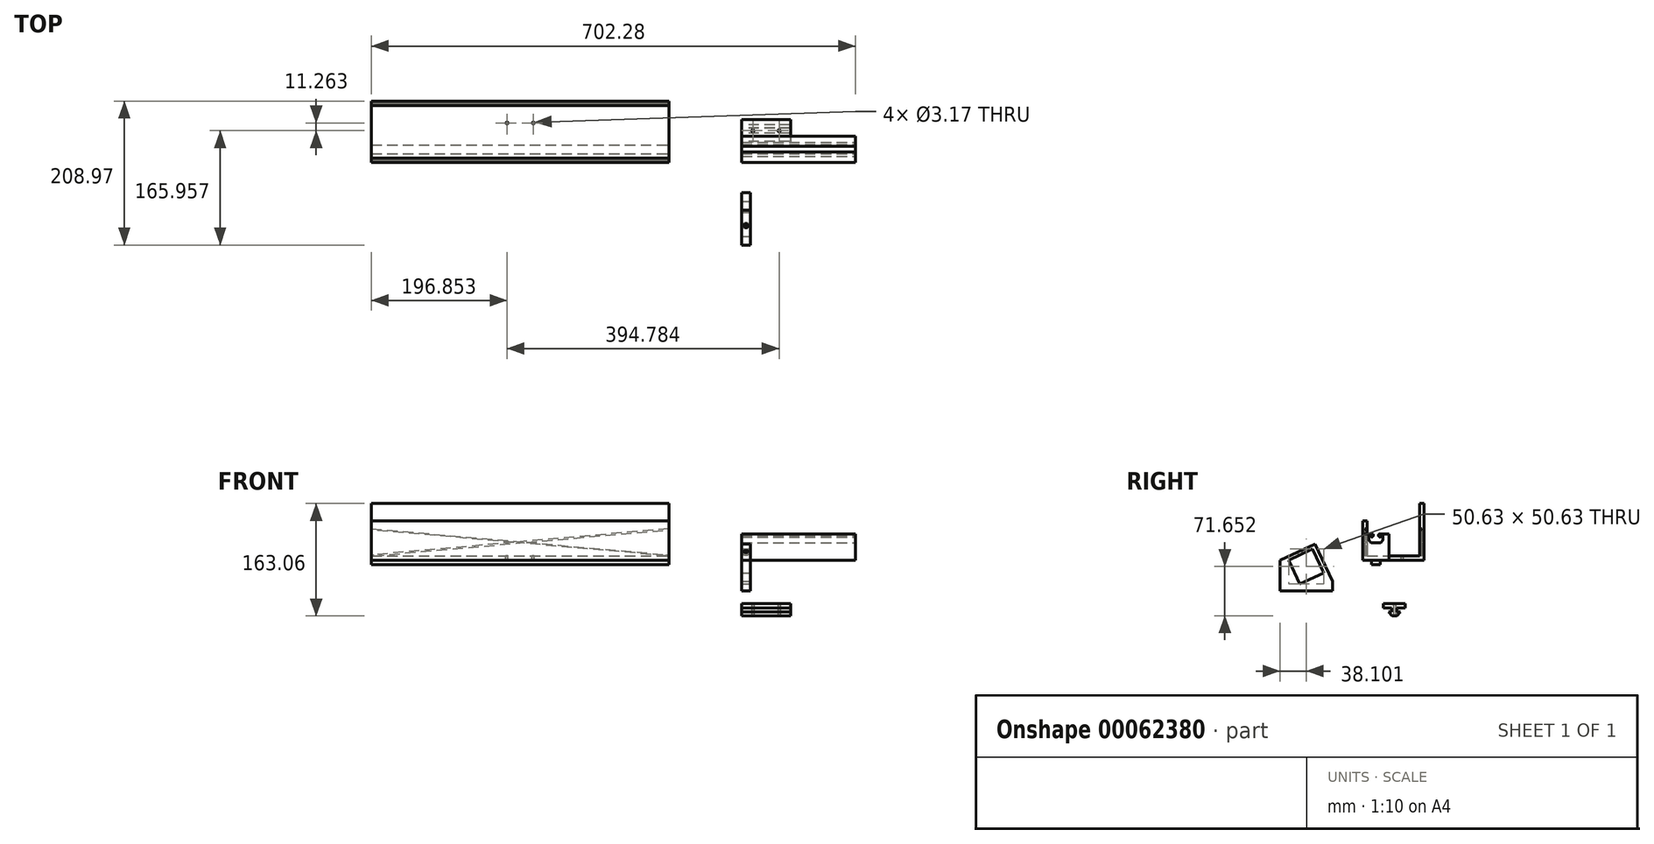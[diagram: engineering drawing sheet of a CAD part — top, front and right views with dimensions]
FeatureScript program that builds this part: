
annotation { "Feature Type Name" : "Feature", "Feature Type Description" : "" }
export const myFeature = defineFeature(function(context is Context, id is Id, definition is map)
    precondition{}
    {
        {
            var Q0;
            Q0=qCreatedBy(makeId("Right.planeOp"),FACE);
            var sketch = newSketch(context, id + "F0", { "sketchPlane" : qUnion([Q0])});
            skLineSegment(sketch, "E0.bottom", {"start": v(0, 0) * mm, "end": v(38.1, 0) * mm});
            skLineSegment(sketch, "E0.top", {"start": v(0, 38.1) * mm, "end": v(38.1, 38.1) * mm});
            skLineSegment(sketch, "E0.left", {"start": v(0, 0) * mm, "end": v(0, 38.1) * mm});
            skLineSegment(sketch, "E0.right", {"start": v(38.1, 0) * mm, "end": v(38.1, 38.1) * mm});
            skSolve(sketch);
        }
        {
            var Q0;
            Q0=makeQuery(id+"F0.imprint","IMPRINT",FACE,{"disambiguationData":[TD([[makeQuery(id+"F0.imprint","IMPRINT",EDGE,{"derivedFrom":sQuery(id+"F0.wireOp",EDGE,"E0.bottom")}),1.0]])]});
            extrude(context, id + "F1", {"entities" : qUnion([Q0]), "depth" : 165.1 * mm});
        }
        {
            var Q0;
            Q0=qCreatedBy(makeId("Top.planeOp"),FACE);
            var sketch = newSketch(context, id + "F2", { "sketchPlane" : qUnion([Q0])});
            skLineSegment(sketch, "E1.bottom", {"start": v(-105.38, 0) * mm, "end": v(-537.18, 0) * mm});
            skLineSegment(sketch, "E1.top", {"start": v(-105.38, 88.9) * mm, "end": v(-537.18, 88.9) * mm});
            skLineSegment(sketch, "E1.left", {"start": v(-105.38, 0) * mm, "end": v(-105.38, 88.9) * mm});
            skLineSegment(sketch, "E1.right", {"start": v(-537.18, 0) * mm, "end": v(-537.18, 88.9) * mm});
            skLineSegment(sketch, "E2", {"start": v(-537.18, 82.55) * mm, "end": v(-105.38, 82.55) * mm});
            skLineSegment(sketch, "E3", {"start": v(-537.18, 6.35) * mm, "end": v(-105.38, 6.35) * mm});
            skSolve(sketch);
        }
        {
            var Q0;
            Q0=qSketchRegion(id+"F2",true);
            extrude(context, id + "F3", {"entities" : qUnion([Q0]), "depth" : 6.35 * mm});
        }
        {
            var Q0;
            Q0=makeQuery(id+"F3.opExtrude","CAP_FACE",FACE,{"disambiguationData":[OSD([sQuery(id+"F2.wireOp",EDGE,"E1.bottom"),sQuery(id+"F2.wireOp",EDGE,"E1.top"),sQuery(id+"F2.wireOp",EDGE,"E1.left"),sQuery(id+"F2.wireOp",EDGE,"E1.right")])],"isStart":false});
            var sketch = newSketch(context, id + "F4", { "sketchPlane" : qUnion([Q0])});
            skLineSegment(sketch, "E4.bottom", {"start": v(-537.18, 88.9) * mm, "end": v(-105.38, 88.9) * mm});
            skLineSegment(sketch, "E4.top", {"start": v(-537.18, 82.55) * mm, "end": v(-105.38, 82.55) * mm});
            skLineSegment(sketch, "E4.left", {"start": v(-537.18, 88.9) * mm, "end": v(-537.18, 82.55) * mm});
            skLineSegment(sketch, "E4.right", {"start": v(-105.38, 88.9) * mm, "end": v(-105.38, 82.55) * mm});
            skSolve(sketch);
        }
        {
            var Q0;
            Q0=makeQuery(id+"F4.imprint","IMPRINT",FACE,{"disambiguationData":[TD([[makeQuery(id+"F4.imprint","IMPRINT",EDGE,{"derivedFrom":sQuery(id+"F4.wireOp",EDGE,"E4.bottom")}),1.0]])]});
            extrude(context, id + "F5", {"entities" : qUnion([Q0]), "operationType" : NewBodyOperationType.ADD, "depth" : 76.2 * mm});
        }
        {
            var Q0;
            Q0=makeQuery(id+"F3.opExtrude","CAP_FACE",FACE,{"disambiguationData":[OSD([sQuery(id+"F2.wireOp",EDGE,"E1.bottom"),sQuery(id+"F2.wireOp",EDGE,"E1.top"),sQuery(id+"F2.wireOp",EDGE,"E1.left"),sQuery(id+"F2.wireOp",EDGE,"E1.right")])],"isStart":false});
            var sketch = newSketch(context, id + "F6", { "sketchPlane" : qUnion([Q0])});
            skLineSegment(sketch, "E5.bottom", {"start": v(-537.18, 0) * mm, "end": v(-105.38, 0) * mm});
            skLineSegment(sketch, "E5.top", {"start": v(-537.18, 6.35) * mm, "end": v(-105.38, 6.35) * mm});
            skLineSegment(sketch, "E5.left", {"start": v(-537.18, 0) * mm, "end": v(-537.18, 6.35) * mm});
            skLineSegment(sketch, "E5.right", {"start": v(-105.38, 0) * mm, "end": v(-105.38, 6.35) * mm});
            skSolve(sketch);
        }
        {
            var Q0;
            Q0=makeQuery(id+"F6.imprint","IMPRINT",FACE,{"disambiguationData":[TD([[makeQuery(id+"F6.imprint","IMPRINT",EDGE,{"derivedFrom":sQuery(id+"F6.wireOp",EDGE,"E5.bottom")}),-1.0]])]});
            extrude(context, id + "F7", {"entities" : qUnion([Q0]), "operationType" : NewBodyOperationType.ADD, "depth" : 50.8 * mm});
        }
        {
            var Q0;
            Q0=makeQuery(id+"F5.opExtrude","SWEPT_FACE",FACE,{"disambiguationData":[OSD([sQuery(id+"F4.wireOp",EDGE,"E4.top")])]});
            var sketch = newSketch(context, id + "F8", { "sketchPlane" : qUnion([Q0])});
            skLineSegment(sketch, "E6", {"start": v(-537.18, 44.45) * mm, "end": v(-105.38, 6.35) * mm});
            skLineSegment(sketch, "E7", {"start": v(-105.38, 6.35) * mm, "end": v(-105.38, 7.94) * mm});
            skLineSegment(sketch, "E8", {"start": v(-105.38, 7.94) * mm, "end": v(-537.18, 46.04) * mm});
            skLineSegment(sketch, "E9", {"start": v(-537.18, 46.04) * mm, "end": v(-537.18, 44.45) * mm});
            skLineSegment(sketch, "E10", {"start": v(-108.54, 8.22) * mm, "end": v(-108.68, 6.64) * mm});
            skLineSegment(sketch, "E11", {"start": v(-321.28, 82.55) * mm, "end": v(-321.28, 6.35) * mm, "construction": true});
            skLineSegment(sketch, "E12.MirrorCS", {"start": v(-537.18, 7.94) * mm, "end": v(-105.38, 46.04) * mm});
            skLineSegment(sketch, "E13.MirrorCS", {"start": v(-105.38, 44.45) * mm, "end": v(-537.18, 6.35) * mm});
            skLineSegment(sketch, "E14.MirrorCS", {"start": v(-534.01, 8.22) * mm, "end": v(-533.87, 6.64) * mm});
            skSolve(sketch);
        }
        {
            var Q0;
            {var subQ0=sQuery(id+"F8.wireOp",EDGE,"E9");Q0=makeQuery(id+"F8.imprint","IMPRINT",FACE,{"disambiguationData":[TD([[makeQuery(id+"F8.imprint","IMPRINT",EDGE,{"derivedFrom":subQ0}),1.0]])]});}
            var Q1;
            {var subQ0=sQuery(id+"F8.wireOp",EDGE,"E13.MirrorCS");var subQ1=sQuery(id+"F8.wireOp",EDGE,"E8");var subQ2=makeQuery(id+"F8.imprint","INTERSECT",VERTEX,{"derivedFrom":[subQ1,subQ0]});Q1=makeQuery(id+"F8.imprint","IMPRINT",FACE,{"disambiguationData":[TD([[makeQuery(id+"F8.imprint","IMPRINT",EDGE,{"disambiguationData":[TD([[subQ2,-1.0]])],"derivedFrom":subQ1}),-1.0]])]});}
            var Q2;
            {var subQ0=sQuery(id+"F8.wireOp",EDGE,"E10");Q2=makeQuery(id+"F8.imprint","IMPRINT",FACE,{"disambiguationData":[TD([[makeQuery(id+"F8.imprint","IMPRINT",EDGE,{"derivedFrom":subQ0}),-1.0]])]});}
            var Q3;
            {var subQ0=sQuery(id+"F8.wireOp",EDGE,"E12.MirrorCS");var subQ1=sQuery(id+"F8.wireOp",EDGE,"E6");var subQ2=makeQuery(id+"F8.imprint","INTERSECT",VERTEX,{"derivedFrom":[subQ1,subQ0]});Q3=makeQuery(id+"F8.imprint","IMPRINT",FACE,{"disambiguationData":[TD([[makeQuery(id+"F8.imprint","IMPRINT",EDGE,{"disambiguationData":[TD([[subQ2,-1.0]])],"derivedFrom":subQ1}),1.0]])]});}
            var Q4;
            {var subQ5=sQuery(id+"F8.wireOp",EDGE,"E14.MirrorCS");Q4=makeQuery(id+"F8.imprint","IMPRINT",FACE,{"disambiguationData":[TD([[makeQuery(id+"F8.imprint","IMPRINT",EDGE,{"derivedFrom":subQ5}),1.0]])]});}
            extrude(context, id + "F9", {"entities" : qUnion([Q0, Q1, Q2, Q3, Q4]), "operationType" : NewBodyOperationType.REMOVE, "oppositeDirection" : true, "depth" : 3.17 * mm, "hasSecondDirection" : true, "secondDirectionOppositeDirection" : false, "secondDirectionDepth" : 79.38 * mm});
        }
        {
            var Q0;
            Q0=makeQuery(id+"F3.opExtrude","CAP_FACE",FACE,{"disambiguationData":[OSD([sQuery(id+"F2.wireOp",EDGE,"E1.bottom"),sQuery(id+"F2.wireOp",EDGE,"E1.top"),sQuery(id+"F2.wireOp",EDGE,"E1.left"),sQuery(id+"F2.wireOp",EDGE,"E1.right")])],"isStart":true});
            var sketch = newSketch(context, id + "F10", { "sketchPlane" : qUnion([Q0])});
            skLineSegment(sketch, "E15.bottom", {"start": v(-537.18, -25.4) * mm, "end": v(-105.38, -25.4) * mm});
            skLineSegment(sketch, "E15.top", {"start": v(-537.18, -12.7) * mm, "end": v(-105.38, -12.7) * mm});
            skLineSegment(sketch, "E15.left", {"start": v(-537.18, -25.4) * mm, "end": v(-537.18, -12.7) * mm});
            skLineSegment(sketch, "E15.right", {"start": v(-105.38, -25.4) * mm, "end": v(-105.38, -12.7) * mm});
            skSolve(sketch);
        }
        {
            var Q0;
            Q0=makeQuery(id+"F10.imprint","IMPRINT",FACE,{"disambiguationData":[TD([[makeQuery(id+"F10.imprint","IMPRINT",EDGE,{"derivedFrom":sQuery(id+"F10.wireOp",EDGE,"E15.bottom")}),1.0]])]});
            extrude(context, id + "F11", {"entities" : qUnion([Q0]), "operationType" : NewBodyOperationType.ADD, "depth" : 6.35 * mm});
        }
        {
            var Q0;
            Q0=qCreatedBy(makeId("Right.planeOp"),FACE);
            var sketch = newSketch(context, id + "F12", { "sketchPlane" : qUnion([Q0])});
            skLineSegment(sketch, "E16", {"start": v(-43.87, 0) * mm, "end": v(-43.87, 35.53) * mm});
            skLineSegment(sketch, "E17", {"start": v(-43.87, 35.53) * mm, "end": v(-120.07, 0) * mm});
            skLineSegment(sketch, "E18", {"start": v(-120.07, 0) * mm, "end": v(-43.87, 0) * mm});
            skSolve(sketch);
        }
        {
            var Q0;
            Q0=makeQuery(id+"F12.imprint","IMPRINT",FACE,{"disambiguationData":[TD([[makeQuery(id+"F12.imprint","IMPRINT",EDGE,{"derivedFrom":sQuery(id+"F12.wireOp",EDGE,"E16")}),1.0]])]});
            extrude(context, id + "F13", {"entities" : qUnion([Q0]), "depth" : 12.7 * mm});
        }
        {
            var Q0;
            Q0=makeQuery(id+"F13.opExtrude","SWEPT_FACE",FACE,{"disambiguationData":[OSD([sQuery(id+"F12.wireOp",EDGE,"E18")])]});
            extrude(context, id + "F14", {"entities" : qUnion([Q0]), "operationType" : NewBodyOperationType.ADD, "depth" : 44.45 * mm});
        }
        {
            var Q0;
            {var subQ0=sQuery(id+"F12.wireOp",EDGE,"E18");Q0=makeQuery(id+"F14.boolean.opBoolean","MERGE",FACE,{"derivedFrom":[makeQuery(id+"F13.opExtrude","CAP_FACE",FACE,{"disambiguationData":[OSD([sQuery(id+"F12.wireOp",EDGE,"E16"),sQuery(id+"F12.wireOp",EDGE,"E17"),subQ0])],"isStart":false}),makeQuery(id+"F14.opExtrude","SWEPT_FACE",FACE,{"disambiguationData":[OSD([subQ0]),TDD([makeQuery(id+"F13.opExtrude","CAP_EDGE",EDGE,{"disambiguationData":[OSD([subQ0])],"isStart":false})])]})]});}
            var sketch = newSketch(context, id + "F15", { "sketchPlane" : qUnion([Q0])});
            skLineSegment(sketch, "E19", {"start": v(-72.75, 16.46) * mm, "end": v(-56.65, -18.07) * mm});
            skLineSegment(sketch, "E20", {"start": v(-56.65, -18.07) * mm, "end": v(-91.18, -34.17) * mm});
            skLineSegment(sketch, "E21", {"start": v(-91.18, -34.17) * mm, "end": v(-107.29, 0.36) * mm});
            skLineSegment(sketch, "E22", {"start": v(-107.29, 0.36) * mm, "end": v(-72.75, 16.46) * mm});
            skLineSegment(sketch, "E23", {"start": v(-107.29, 0.36) * mm, "end": v(-120.07, 0.36) * mm, "construction": true});
            skLineSegment(sketch, "E24", {"start": v(-56.65, -18.07) * mm, "end": v(-43.87, -18.07) * mm, "construction": true});
            skSolve(sketch);
        }
        {
            var Q0;
            Q0=makeQuery(id+"F15.imprint","IMPRINT",FACE,{"disambiguationData":[TD([[makeQuery(id+"F15.imprint","IMPRINT",EDGE,{"derivedFrom":sQuery(id+"F15.wireOp",EDGE,"E19")}),-1.0]])]});
            extrude(context, id + "F16", {"entities" : qUnion([Q0]), "operationType" : NewBodyOperationType.REMOVE, "endBound" : BoundingType.UP_TO_NEXT, "oppositeDirection" : true, "depth" : 25.4 * mm});
        }
        {
            var Q0;
            Q0=makeQuery(id+"F16.boolean.opBoolean","COPY",FACE,{"derivedFrom":makeQuery(id+"F16.opExtrude","SWEPT_FACE",FACE,{"disambiguationData":[OSD([sQuery(id+"F15.wireOp",EDGE,"E22")])]})});
            var sketch = newSketch(context, id + "F17", { "sketchPlane" : qUnion([Q0])});
            skPoint(sketch, "E25.centerSnap0", {"position": v(12.7, 78.03) * mm});
            skCircle(sketch, "E26", {"center": v(6.35, 78.03) * mm, "radius": 3.18 * mm});
            skSolve(sketch);
        }
        {
            var Q0;
            Q0=makeQuery(id+"F17.imprint","IMPRINT",FACE,{"disambiguationData":[TD([[makeQuery(id+"F17.imprint","IMPRINT",EDGE,{"derivedFrom":sQuery(id+"F17.wireOp",EDGE,"E25")}),1.0]])]});
            var Q1;
            Q1=makeQuery(id+"F17.imprint","IMPRINT",FACE,{"disambiguationData":[TD([[makeQuery(id+"F17.imprint","IMPRINT",EDGE,{"derivedFrom":sQuery(id+"F17.wireOp",EDGE,"E26")}),1.0]])]});
            extrude(context, id + "F18", {"entities" : qUnion([Q0, Q1]), "operationType" : NewBodyOperationType.REMOVE, "endBound" : BoundingType.UP_TO_NEXT, "oppositeDirection" : true, "depth" : 25.4 * mm});
        }
        {
            var Q0;
            Q0=makeQuery(id+"F1.opExtrude","CAP_FACE",FACE,{"disambiguationData":[OSD([sQuery(id+"F0.wireOp",EDGE,"E0.bottom"),sQuery(id+"F0.wireOp",EDGE,"E0.top"),sQuery(id+"F0.wireOp",EDGE,"E0.left"),sQuery(id+"F0.wireOp",EDGE,"E0.right")])],"isStart":false});
            var sketch = newSketch(context, id + "F19", { "sketchPlane" : qUnion([Q0])});
            skLineSegment(sketch, "E27", {"start": v(19.05, 38.1) * mm, "end": v(19.05, 0) * mm, "construction": true});
            skLineSegment(sketch, "E28", {"start": v(19.05, 25.8) * mm, "end": v(12.47, 25.8) * mm});
            skLineSegment(sketch, "E29", {"start": v(12.2, 25.9) * mm, "end": v(8.88, 29.22) * mm});
            skLineSegment(sketch, "E30", {"start": v(8.76, 29.5) * mm, "end": v(8.76, 35.5) * mm});
            skLineSegment(sketch, "E31", {"start": v(9.16, 35.9) * mm, "end": v(11.9, 35.9) * mm});
            skLineSegment(sketch, "E32", {"start": v(12.3, 35.5) * mm, "end": v(12.3, 34.43) * mm});
            skLineSegment(sketch, "E33", {"start": v(12.7, 34.04) * mm, "end": v(13.4, 34.04) * mm});
            skLineSegment(sketch, "E34", {"start": v(14.99, 35.62) * mm, "end": v(14.99, 38.1) * mm});
            skLineSegment(sketch, "E35", {"start": v(14.99, 38.1) * mm, "end": v(19.05, 38.1) * mm});
            skPoint(sketch, "E36.visualSharp", {"position": v(14.99, 34.04) * mm});
            skArc(sketch, "E36.filletArc", {"start": v(13.4, 34.04) * mm, "mid": v(14.52, 34.5) * mm, "end": v(14.99, 35.62) * mm});
            skPoint(sketch, "E37.visualSharp", {"position": v(8.76, 35.9) * mm});
            skArc(sketch, "E37.filletArc", {"start": v(9.16, 35.9) * mm, "mid": v(8.88, 35.77) * mm, "end": v(8.76, 35.5) * mm});
            skPoint(sketch, "E38.visualSharp", {"position": v(8.76, 29.34) * mm});
            skArc(sketch, "E38.filletArc", {"start": v(8.76, 29.5) * mm, "mid": v(8.8, 29.35) * mm, "end": v(8.88, 29.22) * mm});
            skPoint(sketch, "E39.visualSharp", {"position": v(12.3, 25.8) * mm});
            skArc(sketch, "E39.filletArc", {"start": v(12.2, 25.9) * mm, "mid": v(12.32, 25.82) * mm, "end": v(12.47, 25.8) * mm});
            skPoint(sketch, "E40.visualSharp", {"position": v(12.3, 35.9) * mm});
            skArc(sketch, "E40.filletArc", {"start": v(12.3, 35.5) * mm, "mid": v(12.2, 35.77) * mm, "end": v(11.9, 35.9) * mm});
            skPoint(sketch, "E41.visualSharp", {"position": v(12.3, 34.04) * mm});
            skArc(sketch, "E41.filletArc", {"start": v(12.3, 34.43) * mm, "mid": v(12.42, 34.15) * mm, "end": v(12.7, 34.04) * mm});
            skArc(sketch, "E42.MirrorCS", {"start": v(29.34, 29.5) * mm, "mid": v(29.3, 29.35) * mm, "end": v(29.22, 29.22) * mm});
            skArc(sketch, "E43.MirrorCS", {"start": v(25.9, 25.9) * mm, "mid": v(25.78, 25.82) * mm, "end": v(25.63, 25.8) * mm});
            skLineSegment(sketch, "E44.MirrorCS", {"start": v(25.8, 35.5) * mm, "end": v(25.8, 34.43) * mm});
            skArc(sketch, "E45.MirrorCS", {"start": v(25.8, 34.43) * mm, "mid": v(25.68, 34.15) * mm, "end": v(25.4, 34.04) * mm});
            skLineSegment(sketch, "E46.MirrorCS", {"start": v(25.4, 34.04) * mm, "end": v(24.7, 34.04) * mm});
            skArc(sketch, "E47.MirrorCS", {"start": v(25.8, 35.5) * mm, "mid": v(25.9, 35.77) * mm, "end": v(26.2, 35.9) * mm});
            skArc(sketch, "E48.MirrorCS", {"start": v(28.94, 35.9) * mm, "mid": v(29.22, 35.77) * mm, "end": v(29.34, 35.5) * mm});
            skPoint(sketch, "E49.MirrorP", {"position": v(29.34, 29.34) * mm});
            skLineSegment(sketch, "E50.MirrorCS", {"start": v(28.94, 35.9) * mm, "end": v(26.2, 35.9) * mm});
            skLineSegment(sketch, "E51.MirrorCS", {"start": v(23.11, 35.62) * mm, "end": v(23.11, 38.1) * mm});
            skPoint(sketch, "E52.MirrorP", {"position": v(25.8, 25.8) * mm});
            skLineSegment(sketch, "E53.MirrorCS", {"start": v(29.34, 29.5) * mm, "end": v(29.34, 35.5) * mm});
            skPoint(sketch, "E54.MirrorP", {"position": v(29.34, 35.9) * mm});
            skLineSegment(sketch, "E55.MirrorCS", {"start": v(25.9, 25.9) * mm, "end": v(29.22, 29.22) * mm});
            skLineSegment(sketch, "E56.MirrorCS", {"start": v(19.05, 25.8) * mm, "end": v(25.63, 25.8) * mm});
            skLineSegment(sketch, "E57.MirrorCS", {"start": v(23.11, 38.1) * mm, "end": v(19.05, 38.1) * mm});
            skArc(sketch, "E58.MirrorCS", {"start": v(24.7, 34.04) * mm, "mid": v(23.58, 34.5) * mm, "end": v(23.11, 35.62) * mm});
            skPoint(sketch, "E59.MirrorP", {"position": v(25.8, 34.04) * mm});
            skPoint(sketch, "E60.MirrorP", {"position": v(25.8, 35.9) * mm});
            skPoint(sketch, "E61.MirrorP", {"position": v(23.11, 34.04) * mm});
            skSolve(sketch);
        }
        {
            var Q0;
            Q0=makeQuery(id+"F19.imprint","IMPRINT",FACE,{"disambiguationData":[TD([[makeQuery(id+"F19.imprint","IMPRINT",EDGE,{"derivedFrom":sQuery(id+"F19.wireOp",EDGE,"E28")}),-1.0]])]});
            extrude(context, id + "F20", {"entities" : qUnion([Q0]), "operationType" : NewBodyOperationType.REMOVE, "endBound" : BoundingType.UP_TO_NEXT, "oppositeDirection" : true, "depth" : 25.4 * mm});
        }
        {
            var Q0;
            Q0=makeQuery(id+"F20.boolean.opBoolean","COPY",EDGE,{"derivedFrom":makeQuery(id+"F20.opExtrude","SWEPT_EDGE",EDGE,{"disambiguationData":[OSD([sQuery(id+"F0.wireOp",EDGE,"E0.top"),sQuery(id+"F19.wireOp",EDGE,"E34"),sQuery(id+"F19.wireOp",EDGE,"E35")])]})});
            var Q1;
            Q1=makeQuery(id+"F20.boolean.opBoolean","COPY",EDGE,{"derivedFrom":makeQuery(id+"F20.opExtrude","SWEPT_EDGE",EDGE,{"disambiguationData":[OSD([sQuery(id+"F0.wireOp",EDGE,"E0.top"),sQuery(id+"F19.wireOp",EDGE,"E51.MirrorCS"),sQuery(id+"F19.wireOp",EDGE,"E57.MirrorCS")])]})});
            fillet(context, id + "F21", {"entities" : qUnion([Q0, Q1]), "radius" : 0.8 * mm, "tangentPropagation" : true, "allowEdgeOverflow" : false});
        }
        {
            var Q0;
            Q0=qCreatedBy(makeId("Right.planeOp"),FACE);
            var sketch = newSketch(context, id + "F22", { "sketchPlane" : qUnion([Q0])});
            skLineSegment(sketch, "E62", {"start": v(30.01, -62.73) * mm, "end": v(61.76, -62.73) * mm});
            skLineSegment(sketch, "E63", {"start": v(61.76, -62.73) * mm, "end": v(61.76, -68.82) * mm});
            skLineSegment(sketch, "E64", {"start": v(61.76, -68.82) * mm, "end": v(49.7, -68.82) * mm});
            skLineSegment(sketch, "E65", {"start": v(49.7, -68.82) * mm, "end": v(49.7, -74.92) * mm});
            skLineSegment(sketch, "E66", {"start": v(49.7, -74.92) * mm, "end": v(54.46, -74.92) * mm});
            skLineSegment(sketch, "E67", {"start": v(54.46, -74.92) * mm, "end": v(49.32, -80.5) * mm});
            skLineSegment(sketch, "E68", {"start": v(49.32, -80.5) * mm, "end": v(42.46, -80.5) * mm});
            skLineSegment(sketch, "E69", {"start": v(42.46, -80.5) * mm, "end": v(37.31, -74.92) * mm});
            skLineSegment(sketch, "E70", {"start": v(37.31, -74.92) * mm, "end": v(42.08, -74.92) * mm});
            skLineSegment(sketch, "E71", {"start": v(42.08, -74.92) * mm, "end": v(42.08, -68.82) * mm});
            skLineSegment(sketch, "E72", {"start": v(42.08, -68.82) * mm, "end": v(30.01, -68.82) * mm});
            skLineSegment(sketch, "E73", {"start": v(30.01, -68.82) * mm, "end": v(30.01, -62.73) * mm});
            skSolve(sketch);
        }
        {
            var Q0;
            Q0=makeQuery(id+"F22.imprint","IMPRINT",FACE,{"disambiguationData":[TD([[makeQuery(id+"F22.imprint","IMPRINT",EDGE,{"derivedFrom":sQuery(id+"F22.wireOp",EDGE,"E62")}),-1.0]])]});
            extrude(context, id + "F23", {"entities" : qUnion([Q0]), "depth" : 71.12 * mm});
        }
        {
            var Q0;
            Q0=makeQuery(id+"F23.opExtrude","SWEPT_FACE",FACE,{"disambiguationData":[OSD([sQuery(id+"F22.wireOp",EDGE,"E68")])]});
            var sketch = newSketch(context, id + "F24", { "sketchPlane" : qUnion([Q0])});
            skCircle(sketch, "E74", {"center": v(54.46, -45.89) * mm, "radius": 1.59 * mm});
            skPoint(sketch, "E74.centerSnap0", {"position": v(71.12, -45.89) * mm});
            skCircle(sketch, "E75", {"center": v(16.36, -45.89) * mm, "radius": 1.59 * mm});
            skPoint(sketch, "E75.centerSnap0", {"position": v(0, -45.89) * mm});
            skSolve(sketch);
        }
        {
            var Q0;
            Q0=makeQuery(id+"F24.imprint","IMPRINT",FACE,{"disambiguationData":[TD([[makeQuery(id+"F24.imprint","IMPRINT",EDGE,{"derivedFrom":sQuery(id+"F24.wireOp",EDGE,"E74")}),1.0]])]});
            var Q1;
            Q1=makeQuery(id+"F24.imprint","IMPRINT",FACE,{"disambiguationData":[TD([[makeQuery(id+"F24.imprint","IMPRINT",EDGE,{"derivedFrom":sQuery(id+"F24.wireOp",EDGE,"E75")}),1.0]])]});
            extrude(context, id + "F25", {"entities" : qUnion([Q0, Q1]), "operationType" : NewBodyOperationType.REMOVE, "endBound" : BoundingType.UP_TO_NEXT, "oppositeDirection" : true, "depth" : 25.4 * mm});
        }
        {
            var Q0;
            Q0=makeQuery(id+"F3.opExtrude","CAP_FACE",FACE,{"disambiguationData":[OSD([sQuery(id+"F2.wireOp",EDGE,"E1.bottom"),sQuery(id+"F2.wireOp",EDGE,"E1.top"),sQuery(id+"F2.wireOp",EDGE,"E1.left"),sQuery(id+"F2.wireOp",EDGE,"E1.right")])],"isStart":false});
            var sketch = newSketch(context, id + "F26", { "sketchPlane" : qUnion([Q0])});
            skCircle(sketch, "E76", {"center": v(-302.23, 57.15) * mm, "radius": 1.59 * mm});
            skCircle(sketch, "E77", {"center": v(-340.33, 57.15) * mm, "radius": 1.59 * mm});
            skSolve(sketch);
        }
        {
            var Q0;
            Q0=qSketchRegion(id+"F26",true);
            extrude(context, id + "F27", {"entities" : qUnion([Q0]), "operationType" : NewBodyOperationType.REMOVE, "endBound" : BoundingType.UP_TO_NEXT, "oppositeDirection" : true, "depth" : 25.4 * mm});
        }
        {
            var Q0;
            {var subQ0=sQuery(id+"F12.wireOp",EDGE,"E18");Q0=makeQuery(id+"F14.boolean.opBoolean","MERGE",FACE,{"derivedFrom":[makeQuery(id+"F13.opExtrude","CAP_FACE",FACE,{"disambiguationData":[OSD([sQuery(id+"F12.wireOp",EDGE,"E16"),sQuery(id+"F12.wireOp",EDGE,"E17"),subQ0])],"isStart":false}),makeQuery(id+"F14.opExtrude","SWEPT_FACE",FACE,{"disambiguationData":[OSD([subQ0]),TDD([makeQuery(id+"F13.opExtrude","CAP_EDGE",EDGE,{"disambiguationData":[OSD([subQ0])],"isStart":false})])]})]});}
            var sketch = newSketch(context, id + "F28", { "sketchPlane" : qUnion([Q0])});
            skLineSegment(sketch, "E78", {"start": v(-69.15, 23.75) * mm, "end": v(-43.87, -30.46) * mm});
            skSolve(sketch);
        }
        {
            var Q0;
            {var subQ0=sQuery(id+"F28.wireOp",EDGE,"E78");Q0=makeQuery(id+"F28.imprint","IMPRINT",FACE,{"disambiguationData":[TD([[makeQuery(id+"F28.imprint","IMPRINT",EDGE,{"derivedFrom":subQ0}),1.0]])]});}
            extrude(context, id + "F29", {"entities" : qUnion([Q0]), "operationType" : NewBodyOperationType.REMOVE, "endBound" : BoundingType.UP_TO_NEXT, "oppositeDirection" : true, "depth" : 25.4 * mm});
        }
    });
